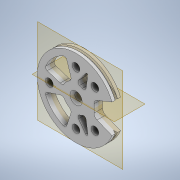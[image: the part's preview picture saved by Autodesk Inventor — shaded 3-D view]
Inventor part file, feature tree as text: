
AUTODESK INVENTOR PART (.ipt)
format: ipt  version: 2020 (Build 240168000, 168)  size: 394,752 bytes
history: native  units: mm
features: sketch x14, extrude x13, projected_geometry x12, other x7, fillet x5, plane x4, reference x4, revolve x1, chamfer x1, mirror x1
ambient origin geometry x8: Origin, YZ Plane, XZ Plane, XY Plane, X Axis, Y Axis, Z Axis, Center Point
bodies: Solid1 (feature_tree)
feature tree (62):
  extrude  "Extrusion1"  Depth=3.5mm TaperAngle=0.0deg
  sketch  "Sketch2"  dims[d3=8.0mm d4=3.5mm d5=0.0mm]
  plane  "Work Plane1"
  extrude  "Extrusion2"  Depth=3.5mm TaperAngle=0.0deg
  extrude  "Extrusion3"  Depth=20.0mm TaperAngle=0.0deg
  plane  "Work Plane2"
  extrude  "Extrusion4"  Depth=10.0mm
  plane  "Work Plane3"
  revolve  "Revolution1"  [1 undecoded]
  extrude  "Extrusion5"  Depth=0.5mm
  extrude  "Extrusion6"  Depth=0.5mm
  fillet  "Fillet1"  Radius=20.0mm
  extrude  "Extrusion7"  TaperAngle=45.0deg  [1 undecoded]
  extrude  "Extrusion8"  Depth=11.0mm
  extrude  "Extrusion9"  Depth=11.0mm
  extrude  "Extrusion10"  Depth=20.0mm TaperAngle=0.0deg
  extrude  "Extrusion11"  Depth=3.839724mm
  extrude  "Extrusion12"  Depth=2.0mm
  fillet  "Fillet2"  Radius=0.7mm
  chamfer  "Chamfer1"  Distance=20.0mm
  extrude  "Extrusion13"  Depth=1.5mm TaperAngle=0.0deg
  fillet  "Fillet3"  Radius=11.0mm
  fillet  "Fillet4"  Radius=3.2mm
  plane  "Work Plane4"
  mirror  "Mirror1"
  fillet  "Fillet5"  Radius=11.0mm
  sketch  "Sketch1"  dims[d0=32.0mm d1=3.5mm d2=0.0mm]
  reference  "Reference1"
  reference  "Reference2"
  reference  "Reference3"
  reference  "Reference4"
  sketch  "Sketch3"  dims[d6=3.0mm d7=20.0mm d8=0.0mm]
  projected_geometry  "Projected Loop1"
  sketch  "Sketch4"  dims[d9=10.0mm d10=3.0mm]
  projected_geometry  "Projected Loop2"
  sketch  "Sketch5"  dims[d11=3.0mm d12=20.0mm d13=0.0mm]
  projected_geometry  "Projected Loop3"
  projected_geometry  "Projected Loop4"
  sketch  "Sketch6"  dims[d14=1.5mm d15=0.5mm]
  projected_geometry  "Projected Loop5"
  sketch  "Sketch7"  dims[d16=0.5mm d17=0.5mm d18=20.0mm]
  projected_geometry  "Projected Loop6"
  sketch  "Sketch8"  dims[d19=90.0deg d20=45.0deg]
  projected_geometry  "Projected Loop7"
  sketch  "Sketch9"  dims[d21=45.0deg d22=11.0mm]
  projected_geometry  "Projected Loop8"
  sketch  "Sketch10"  dims[d23=3.2mm d24=11.0mm]
  sketch  "Sketch11"  dims[d25=3.2mm d26=20.0mm d27=0.0mm]
  projected_geometry  "Projected Loop9"
  sketch  "Sketch12"  dims[d28=3.839724mm d29=3.839724mm]
  projected_geometry  "Projected Loop10"
  sketch  "Sketch13"  dims[d30=20.0mm d31=0.0mm d32=2.0mm d33=0.7mm d34=20.0mm d35=0.0mm]
  projected_geometry  "Projected Loop11"
  sketch  "Sketch14"  dims[d36=0.7mm d37=20.0mm d38=0.0mm d41=11.0mm d42=3.2mm d43=11.0mm d44=3.2mm d45=20.0mm d46=0.0mm d47=20.0mm d48=0.0mm d49=11.0mm d50=3.2mm d51=20.0mm d52=0.0mm d53=27.0mm d54=11.0mm d55=3.141593mm d56=3.141593mm d57=3.141593mm d58=3.141593mm d59=20.0mm d60=0.0mm d61=1.5mm d62=1.0mm d63=1.0mm d64=2.0mm d65=45.0deg d66=11.0mm d67=13.5mm d68=20.0mm d69=0.0mm d70=0.5mm d71=1.0mm d72=1.5mm]
  projected_geometry  "Projected Loop12"
  parser-record x1  (decoder bookkeeping rows leaked as tree rows — omitted from the tree; the rows remain in map.json)
  other  "reducer_1.iam"
  other  "bearing_3_6_2:1"
  other  "tendon_wh_1:1"
  other  "mot_holder_1:1"
  other  "mot_27_ass:1"
  other  "mot_27_1:1"
note: 2 required parameter values undecoded (feature->parameter linkage not recoverable at this tier; creation-order binding heuristic only, values carry confidence <= 0.55)
note: 1 file-system path scrubbed to <path> (originals preserved in map.json)